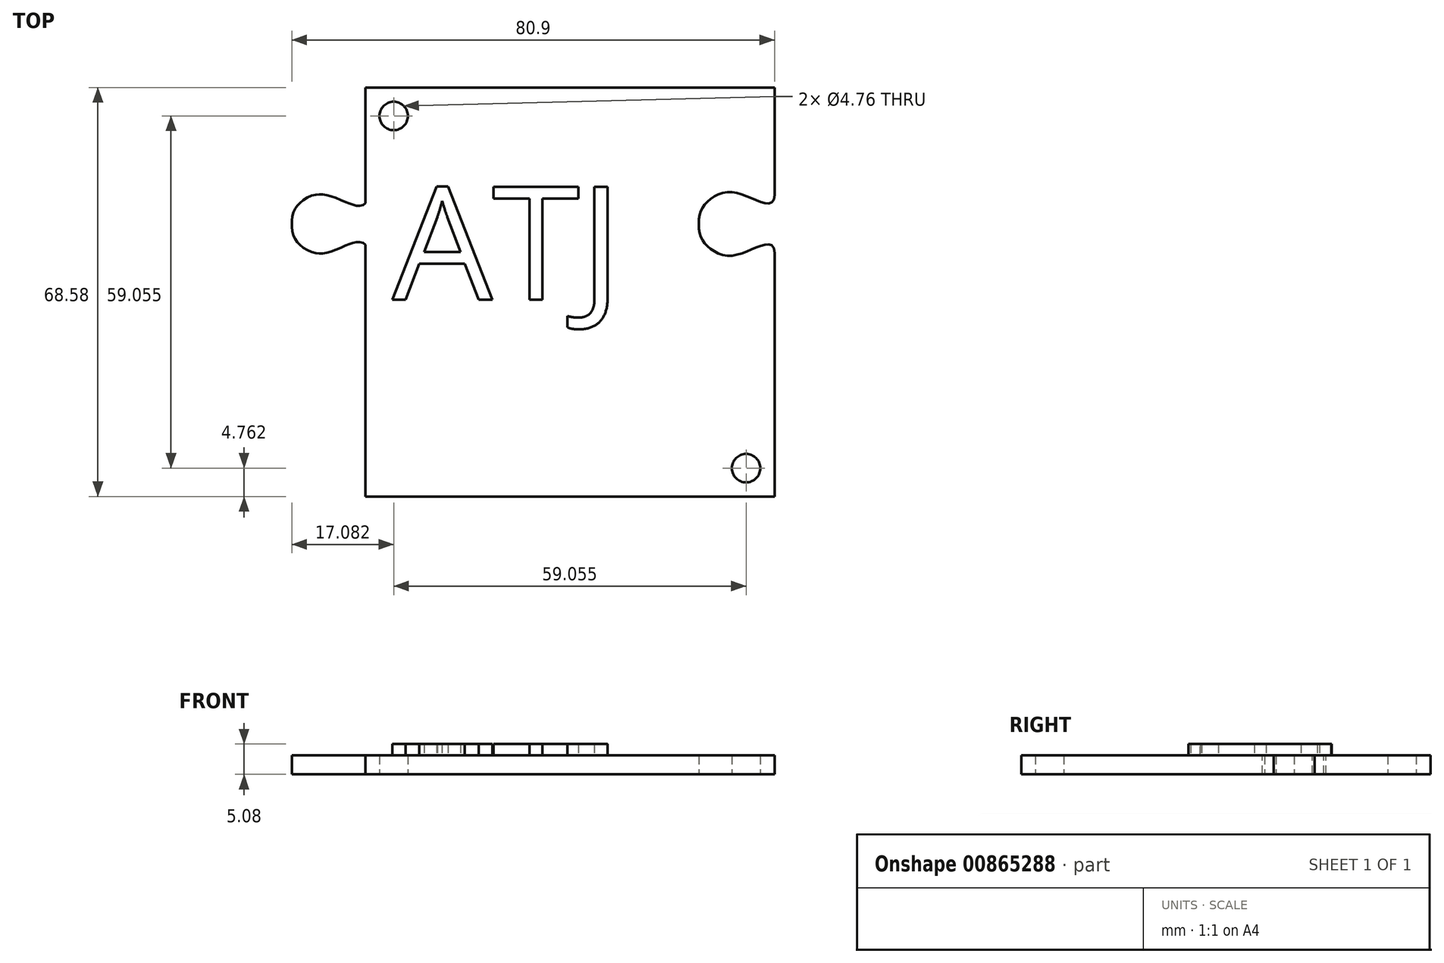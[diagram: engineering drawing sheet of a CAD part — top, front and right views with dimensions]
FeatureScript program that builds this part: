
annotation { "Feature Type Name" : "Feature", "Feature Type Description" : "" }
export const myFeature = defineFeature(function(context is Context, id is Id, definition is map)
    precondition{}
    {
        {
            var Q0;
            Q0=qCreatedBy(makeId("Top.planeOp"),FACE);
            var sketch = newSketch(context, id + "F0", { "sketchPlane" : qUnion([Q0])});
            skLineSegment(sketch, "E0.bottom", {"start": v(34.3, 34.3) * mm, "end": v(-34.3, 34.3) * mm});
            skLineSegment(sketch, "E0.top", {"start": v(34.3, -34.3) * mm, "end": v(-34.3, -34.3) * mm});
            skLineSegment(sketch, "E0.left", {"start": v(34.3, 34.3) * mm, "end": v(34.3, -34.3) * mm});
            skLineSegment(sketch, "E0.right", {"start": v(-34.3, 34.3) * mm, "end": v(-34.3, -34.3) * mm});
            skPoint(sketch, "E0.middle", {"position": v(0, 0) * mm});
            skCircle(sketch, "E1", {"center": v(-29.53, 29.53) * mm, "radius": 2.38 * mm});
            skCircle(sketch, "E2.MirrorC", {"center": v(29.53, -29.53) * mm, "radius": 2.38 * mm});
            skSolve(sketch);
        }
        {
            var Q0;
            Q0=qSketchRegion(id+"F0",true);
            extrude(context, id + "F1", {"entities" : qUnion([Q0]), "depth" : 3.17 * mm});
        }
        {
            var Q0;
            Q0=qCreatedBy(makeId("Top.planeOp"),FACE);
            var sketch = newSketch(context, id + "F2", { "sketchPlane" : qUnion([Q0])});
            skPoint(sketch, "E3", {"position": v(-34.3, 16.33) * mm});
            skPoint(sketch, "E4", {"position": v(-36.2, 14.99) * mm});
            skPoint(sketch, "E5", {"position": v(-41.66, 16.76) * mm});
            skPoint(sketch, "E6", {"position": v(-45.72, 14.99) * mm});
            skPoint(sketch, "E7", {"position": v(-47, 11.43) * mm});
            skFitSpline(sketch, "E8", {"points": [v(-34.3, 16.33) * mm, v(-36.2, 14.99) * mm, v(-41.66, 16.76) * mm, v(-45.72, 14.99) * mm, v(-47, 11.43) * mm], "startDerivative": vector(0, -24.54) * mm, "endDerivative": vector(0, -20.15) * mm});
            skLineSegment(sketch, "E9", {"start": v(-47, 11.43) * mm, "end": v(-29.95, 11.43) * mm, "construction": true});
            skFitSpline(sketch, "E10.MirrorCS", {"points": [v(-34.3, 6.53) * mm, v(-36.2, 7.87) * mm, v(-41.66, 6.1) * mm, v(-45.72, 7.87) * mm, v(-47, 11.43) * mm], "startDerivative": vector(0, 24.54) * mm, "endDerivative": vector(0, 20.15) * mm});
            skLineSegment(sketch, "E11", {"start": v(-34.3, 16.33) * mm, "end": v(-34.3, 6.53) * mm, "construction": true});
            skFitSpline(sketch, "E12.MirrorCS", {"points": [v(-34.3, 16.33) * mm, v(-32.39, 14.99) * mm, v(-26.92, 16.76) * mm, v(-22.86, 14.99) * mm, v(-21.59, 11.43) * mm], "startDerivative": vector(0, -24.54) * mm, "endDerivative": vector(0, -20.15) * mm});
            skFitSpline(sketch, "E13.MirrorCS", {"points": [v(-34.3, 6.53) * mm, v(-32.39, 7.87) * mm, v(-26.92, 6.1) * mm, v(-22.86, 7.87) * mm, v(-21.59, 11.43) * mm], "startDerivative": vector(0, 24.54) * mm, "endDerivative": vector(0, 20.15) * mm});
            skFitSpline(sketch, "E14.0", {"points": [v(-33.9, 6.53) * mm, v(-33.9, 6.8) * mm, v(-33.96, 7.3) * mm, v(-34.16, 7.77) * mm, v(-34.42, 8.07) * mm, v(-34.73, 8.28) * mm, v(-35.16, 8.4) * mm, v(-35.7, 8.38) * mm, v(-36.22, 8.27) * mm, v(-36.76, 8.1) * mm, v(-37.5, 7.83) * mm, v(-38.44, 7.42) * mm, v(-39.6, 6.94) * mm, v(-40.54, 6.64) * mm, v(-41.28, 6.5) * mm, v(-41.8, 6.46) * mm, v(-42.32, 6.5) * mm, v(-43, 6.62) * mm, v(-43.8, 6.91) * mm, v(-44.68, 7.44) * mm, v(-45.29, 7.96) * mm, v(-45.69, 8.4) * mm, v(-46.02, 8.85) * mm, v(-46.33, 9.45) * mm, v(-46.56, 10.3) * mm, v(-46.6, 11.03) * mm, v(-46.6, 11.43) * mm]});
            skFitSpline(sketch, "E14.1", {"points": [v(-33.9, 16.33) * mm, v(-33.9, 16.05) * mm, v(-33.96, 15.56) * mm, v(-34.16, 15.09) * mm, v(-34.42, 14.8) * mm, v(-34.73, 14.58) * mm, v(-35.16, 14.46) * mm, v(-35.7, 14.48) * mm, v(-36.22, 14.6) * mm, v(-36.76, 14.76) * mm, v(-37.5, 15.03) * mm, v(-38.44, 15.44) * mm, v(-39.6, 15.92) * mm, v(-40.54, 16.22) * mm, v(-41.28, 16.36) * mm, v(-41.8, 16.4) * mm, v(-42.32, 16.37) * mm, v(-43, 16.24) * mm, v(-43.8, 15.95) * mm, v(-44.68, 15.42) * mm, v(-45.29, 14.9) * mm, v(-45.69, 14.46) * mm, v(-46.02, 14.01) * mm, v(-46.33, 13.41) * mm, v(-46.56, 12.55) * mm, v(-46.6, 11.83) * mm, v(-46.6, 11.43) * mm]});
            skLineSegment(sketch, "E15", {"start": v(-34.3, 16.33) * mm, "end": v(-34.3, 6.53) * mm});
            skLineSegment(sketch, "E16", {"start": v(-34.3, 7.92) * mm, "end": v(-34.3, 14.94) * mm});
            skFitSpline(sketch, "E17.MirrorCS", {"points": [v(34.3, 16.33) * mm, v(32.39, 14.99) * mm, v(26.92, 16.76) * mm, v(22.86, 14.99) * mm, v(21.59, 11.43) * mm], "startDerivative": vector(0, -24.54) * mm, "endDerivative": vector(0, -20.15) * mm});
            skFitSpline(sketch, "E18.MirrorCS", {"points": [v(34.3, 6.53) * mm, v(32.39, 7.87) * mm, v(26.92, 6.1) * mm, v(22.86, 7.87) * mm, v(21.59, 11.43) * mm], "startDerivative": vector(0, 24.54) * mm, "endDerivative": vector(0, 20.15) * mm});
            skLineSegment(sketch, "E19", {"start": v(34.3, 16.33) * mm, "end": v(39.12, 16.33) * mm});
            skLineSegment(sketch, "E20", {"start": v(39.12, 16.33) * mm, "end": v(39.12, 6.53) * mm});
            skLineSegment(sketch, "E21", {"start": v(39.12, 6.53) * mm, "end": v(34.3, 6.53) * mm});
            skSolve(sketch);
        }
        {
            var Q0;
            Q0=makeQuery(id+"F2.imprint","IMPRINT",FACE,{"disambiguationData":[TD([[makeQuery(id+"F2.imprint","IMPRINT",EDGE,{"derivedFrom":sQuery(id+"F2.wireOp",EDGE,"E14.0")}),-1.0]])]});
            var Q1;
            Q1=makeQuery(id+"F1.opExtrude","CAP_FACE",FACE,{"disambiguationData":[OSD([sQuery(id+"F0.wireOp",EDGE,"E0.bottom"),sQuery(id+"F0.wireOp",EDGE,"E0.top"),sQuery(id+"F0.wireOp",EDGE,"E0.left"),sQuery(id+"F0.wireOp",EDGE,"E0.right"),sQuery(id+"F0.wireOp",EDGE,"E1"),sQuery(id+"F0.wireOp",EDGE,"e1648c08-8adf-473f-9b64-c467cf328ef90.MirrorC"),sQuery(id+"F0.wireOp",EDGE,"1cdcda55-2210-49d8-b5f0-9198a802923b0.MirrorC"),sQuery(id+"F0.wireOp",EDGE,"E2.MirrorC")])],"isStart":false});
            extrude(context, id + "F3", {"entities" : qUnion([Q0]), "operationType" : NewBodyOperationType.ADD, "endBound" : BoundingType.UP_TO_SURFACE, "endBoundEntityFace" : qUnion([Q1]), "depth" : 25.4 * mm});
        }
        {
            var Q0;
            Q0=qCreatedBy(makeId("Right.planeOp"),FACE);
            var sketch = newSketch(context, id + "F4", { "sketchPlane" : qUnion([Q0])});
            skLineSegment(sketch, "E22", {"start": v(0, -65.87) * mm, "end": v(0, 47.63) * mm});
            skSolve(sketch);
        }
        {
            var Q0;
            Q0=makeQuery(id+"F2.imprint","IMPRINT",FACE,{"disambiguationData":[TD([[makeQuery(id+"F2.imprint","IMPRINT",EDGE,{"derivedFrom":sQuery(id+"F2.wireOp",EDGE,"E17.MirrorCS")}),1.0]])]});
            extrude(context, id + "F5", {"entities" : qUnion([Q0]), "operationType" : NewBodyOperationType.REMOVE, "endBound" : BoundingType.THROUGH_ALL, "depth" : 25.4 * mm});
        }
        {
            var Q0;
            Q0=qCreatedBy(makeId("Top.planeOp"),FACE);
            var sketch = newSketch(context, id + "F6", { "sketchPlane" : qUnion([Q0])});
            skText(sketch, "E23", { "text": "ATJ", "fontName": "OpenSans-Regular.ttf"});
            const initialGuessF6  = {"E23": [-0.02978, -0.00127, 1, 0, 0.01908]};
            skSetInitialGuess(sketch, initialGuessF6);
            skSolve(sketch);
        }
        {
            var Q0;
            Q0 = qSketchRegion(id + "F6", true);
            extrude(context, id + "F7", {"entities" : qUnion([Q0]), "operationType" : NewBodyOperationType.ADD, "depth" : 5.08 * mm, "offsetDistance" : 25.4 * mm});
        }
    });
